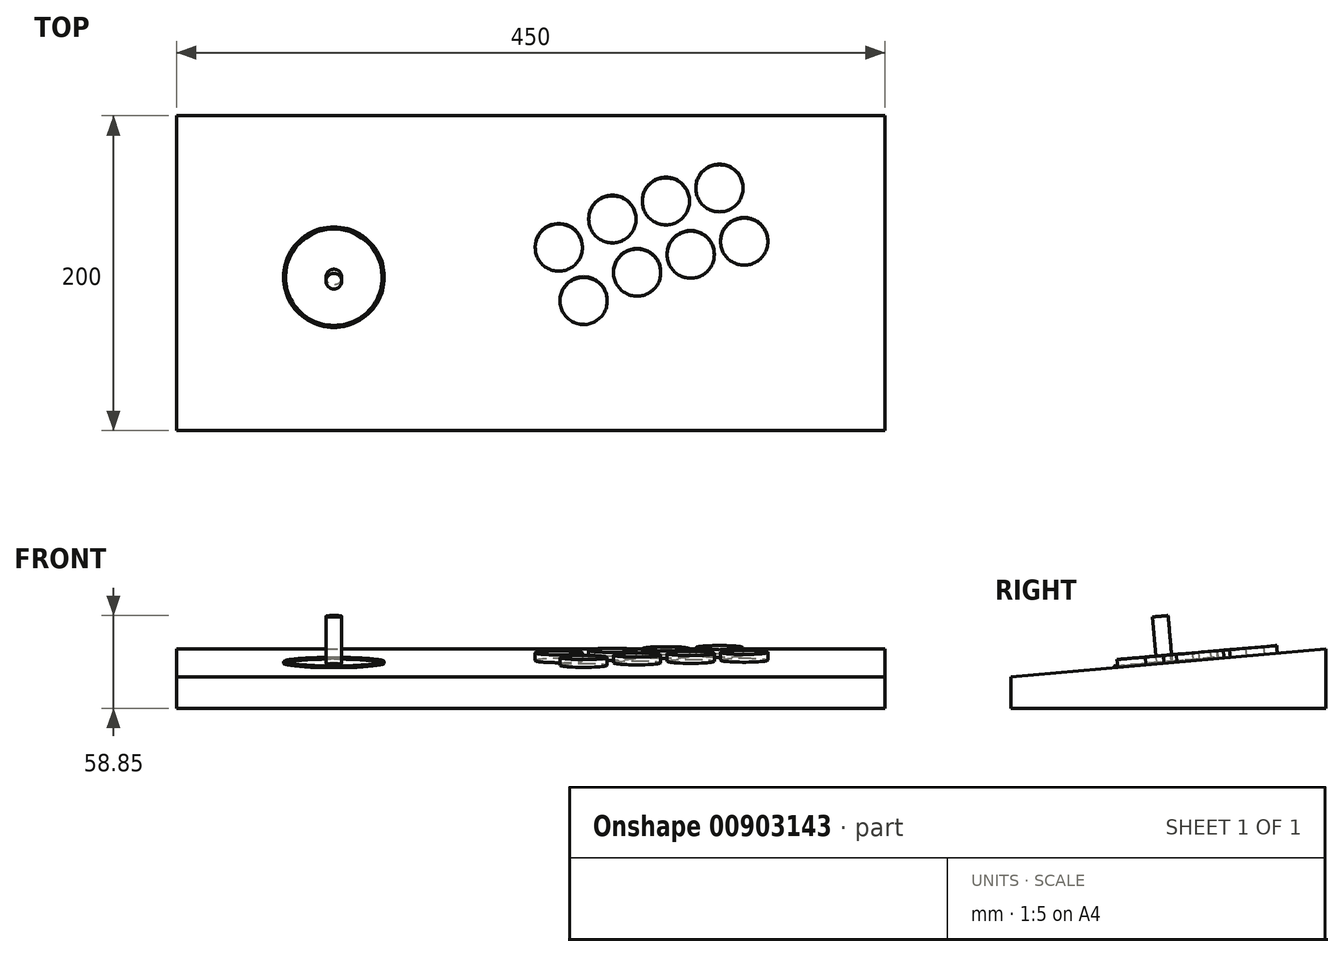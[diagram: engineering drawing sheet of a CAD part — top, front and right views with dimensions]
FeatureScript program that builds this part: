
annotation { "Feature Type Name" : "Feature", "Feature Type Description" : "" }
export const myFeature = defineFeature(function(context is Context, id is Id, definition is map)
    precondition{}
    {
        {
            var Q0;
            Q0=qCreatedBy(makeId("Top.planeOp"),FACE);
            var sketch = newSketch(context, id + "F0", { "sketchPlane" : qUnion([Q0])});
            skLineSegment(sketch, "E0.bottom", {"start": v(225, 100) * mm, "end": v(-225, 100) * mm});
            skLineSegment(sketch, "E0.top", {"start": v(225, -100) * mm, "end": v(-225, -100) * mm});
            skLineSegment(sketch, "E0.left", {"start": v(225, 100) * mm, "end": v(225, -100) * mm});
            skLineSegment(sketch, "E0.right", {"start": v(-225, 100) * mm, "end": v(-225, -100) * mm});
            skPoint(sketch, "E0.middle", {"position": v(0, 0) * mm});
            skSolve(sketch);
        }
        {
            var Q0;
            Q0=makeQuery(id+"F0.imprint","IMPRINT",FACE,{"disambiguationData":[TD([[makeQuery(id+"F0.imprint","IMPRINT",EDGE,{"derivedFrom":sQuery(id+"F0.wireOp",EDGE,"E0.bottom")}),1.0]])]});
            extrude(context, id + "F1", {"entities" : qUnion([Q0]), "depth" : 20 * mm, "offsetDistance" : 25 * mm});
        }
        {
            var Q0;
            Q0=makeQuery(id+"F1.opExtrude","SWEPT_FACE",FACE,{"disambiguationData":[OSD([sQuery(id+"F0.wireOp",EDGE,"E0.left")])]});
            var sketch = newSketch(context, id + "F2", { "sketchPlane" : qUnion([Q0])});
            skLineSegment(sketch, "E1", {"start": v(-100, 20) * mm, "end": v(100, 37.5) * mm});
            skLineSegment(sketch, "E2", {"start": v(100, 37.5) * mm, "end": v(100, 20) * mm});
            skLineSegment(sketch, "E3", {"start": v(100, 20) * mm, "end": v(100, 0) * mm});
            skLineSegment(sketch, "E4", {"start": v(100, 0) * mm, "end": v(-100, 0) * mm});
            skLineSegment(sketch, "E5", {"start": v(-100, 0) * mm, "end": v(-100, 20) * mm});
            skSolve(sketch);
        }
        {
            var Q0;
            Q0=makeQuery(id+"F2.imprint","IMPRINT",FACE,{"disambiguationData":[TD([[makeQuery(id+"F2.imprint","IMPRINT",EDGE,{"derivedFrom":sQuery(id+"F2.wireOp",EDGE,"E1")}),-1.0]])]});
            extrude(context, id + "F3", {"entities" : qUnion([Q0]), "operationType" : NewBodyOperationType.ADD, "oppositeDirection" : true, "depth" : 450 * mm, "offsetDistance" : 25 * mm});
        }
        {
            var Q0;
            Q0=makeQuery(id+"F3.opExtrude","SWEPT_FACE",FACE,{"disambiguationData":[OSD([sQuery(id+"F2.wireOp",EDGE,"E1")])]});
            var sketch = newSketch(context, id + "F4", { "sketchPlane" : qUnion([Q0])});
            skLineSegment(sketch, "E6.bottom", {"start": v(-225, 102.89) * mm, "end": v(225, 102.89) * mm, "construction": true});
            skLineSegment(sketch, "E6.top", {"start": v(-225, -97.88) * mm, "end": v(225, -97.88) * mm, "construction": true});
            skLineSegment(sketch, "E6.left", {"start": v(-225, 102.89) * mm, "end": v(-225, -97.88) * mm, "construction": true});
            skLineSegment(sketch, "E6.right", {"start": v(225, 102.89) * mm, "end": v(225, -97.88) * mm, "construction": true});
            skLineSegment(sketch, "E7", {"start": v(-225, 102.89) * mm, "end": v(-225, 0) * mm});
            skLineSegment(sketch, "E8", {"start": v(-225, 0) * mm, "end": v(-125, 0) * mm, "construction": true});
            skCircle(sketch, "E9", {"center": v(-125, 0) * mm, "radius": 32 * mm});
            skCircle(sketch, "E10", {"center": v(17.89, 19.2) * mm, "radius": 15 * mm});
            skCircle(sketch, "E11", {"center": v(51.89, 37.24) * mm, "radius": 15 * mm});
            skCircle(sketch, "E12", {"center": v(33.6, -14.8) * mm, "radius": 15 * mm});
            skCircle(sketch, "E13", {"center": v(67.6, 3.24) * mm, "radius": 15 * mm});
            skCircle(sketch, "E14", {"center": v(101.6, 14.7) * mm, "radius": 15 * mm});
            skCircle(sketch, "E15", {"center": v(85.89, 48.7) * mm, "radius": 15 * mm});
            skCircle(sketch, "E16", {"center": v(135.6, 23.02) * mm, "radius": 15 * mm});
            skCircle(sketch, "E17", {"center": v(119.89, 57.02) * mm, "radius": 15 * mm});
            skCircle(sketch, "E18", {"center": v(-125, 0) * mm, "radius": 30.75 * mm});
            skCircle(sketch, "E19", {"center": v(-125, 0) * mm, "radius": 5 * mm});
            skSolve(sketch);
        }
        {
            var Q0;
            Q0=makeQuery(id+"F4.imprint","IMPRINT",FACE,{"disambiguationData":[TD([[makeQuery(id+"F4.imprint","IMPRINT",EDGE,{"derivedFrom":sQuery(id+"F4.wireOp",EDGE,"E10")}),1.0]])]});
            var Q1;
            Q1=makeQuery(id+"F4.imprint","IMPRINT",FACE,{"disambiguationData":[TD([[makeQuery(id+"F4.imprint","IMPRINT",EDGE,{"derivedFrom":sQuery(id+"F4.wireOp",EDGE,"E12")}),1.0]])]});
            var Q2;
            Q2=makeQuery(id+"F4.imprint","IMPRINT",FACE,{"disambiguationData":[TD([[makeQuery(id+"F4.imprint","IMPRINT",EDGE,{"derivedFrom":sQuery(id+"F4.wireOp",EDGE,"E11")}),1.0]])]});
            var Q3;
            Q3=makeQuery(id+"F4.imprint","IMPRINT",FACE,{"disambiguationData":[TD([[makeQuery(id+"F4.imprint","IMPRINT",EDGE,{"derivedFrom":sQuery(id+"F4.wireOp",EDGE,"E13")}),1.0]])]});
            var Q4;
            Q4=makeQuery(id+"F4.imprint","IMPRINT",FACE,{"disambiguationData":[TD([[makeQuery(id+"F4.imprint","IMPRINT",EDGE,{"derivedFrom":sQuery(id+"F4.wireOp",EDGE,"E15")}),1.0]])]});
            var Q5;
            Q5=makeQuery(id+"F4.imprint","IMPRINT",FACE,{"disambiguationData":[TD([[makeQuery(id+"F4.imprint","IMPRINT",EDGE,{"derivedFrom":sQuery(id+"F4.wireOp",EDGE,"E14")}),1.0]])]});
            var Q6;
            Q6=makeQuery(id+"F4.imprint","IMPRINT",FACE,{"disambiguationData":[TD([[makeQuery(id+"F4.imprint","IMPRINT",EDGE,{"derivedFrom":sQuery(id+"F4.wireOp",EDGE,"E17")}),1.0]])]});
            var Q7;
            Q7=makeQuery(id+"F4.imprint","IMPRINT",FACE,{"disambiguationData":[TD([[makeQuery(id+"F4.imprint","IMPRINT",EDGE,{"derivedFrom":sQuery(id+"F4.wireOp",EDGE,"E16")}),1.0]])]});
            extrude(context, id + "F5", {"entities" : qUnion([Q0, Q1, Q2, Q3, Q4, Q5, Q6, Q7]), "operationType" : NewBodyOperationType.ADD, "depth" : 5 * mm, "offsetDistance" : 25 * mm});
        }
        {
            var Q0;
            Q0=makeQuery(id+"F4.imprint","IMPRINT",FACE,{"disambiguationData":[TD([[makeQuery(id+"F4.imprint","IMPRINT",EDGE,{"derivedFrom":sQuery(id+"F4.wireOp",EDGE,"E9")}),1.0]])]});
            extrude(context, id + "F6", {"entities" : qUnion([Q0]), "operationType" : NewBodyOperationType.ADD, "depth" : 1 * mm, "offsetDistance" : 25 * mm});
        }
        {
            var Q0;
            Q0=makeQuery(id+"F4.imprint","IMPRINT",FACE,{"disambiguationData":[TD([[makeQuery(id+"F4.imprint","IMPRINT",EDGE,{"derivedFrom":sQuery(id+"F4.wireOp",EDGE,"E19")}),1.0]])]});
            extrude(context, id + "F7", {"entities" : qUnion([Q0]), "operationType" : NewBodyOperationType.ADD, "depth" : 30 * mm, "offsetDistance" : 25 * mm});
        }
    });
